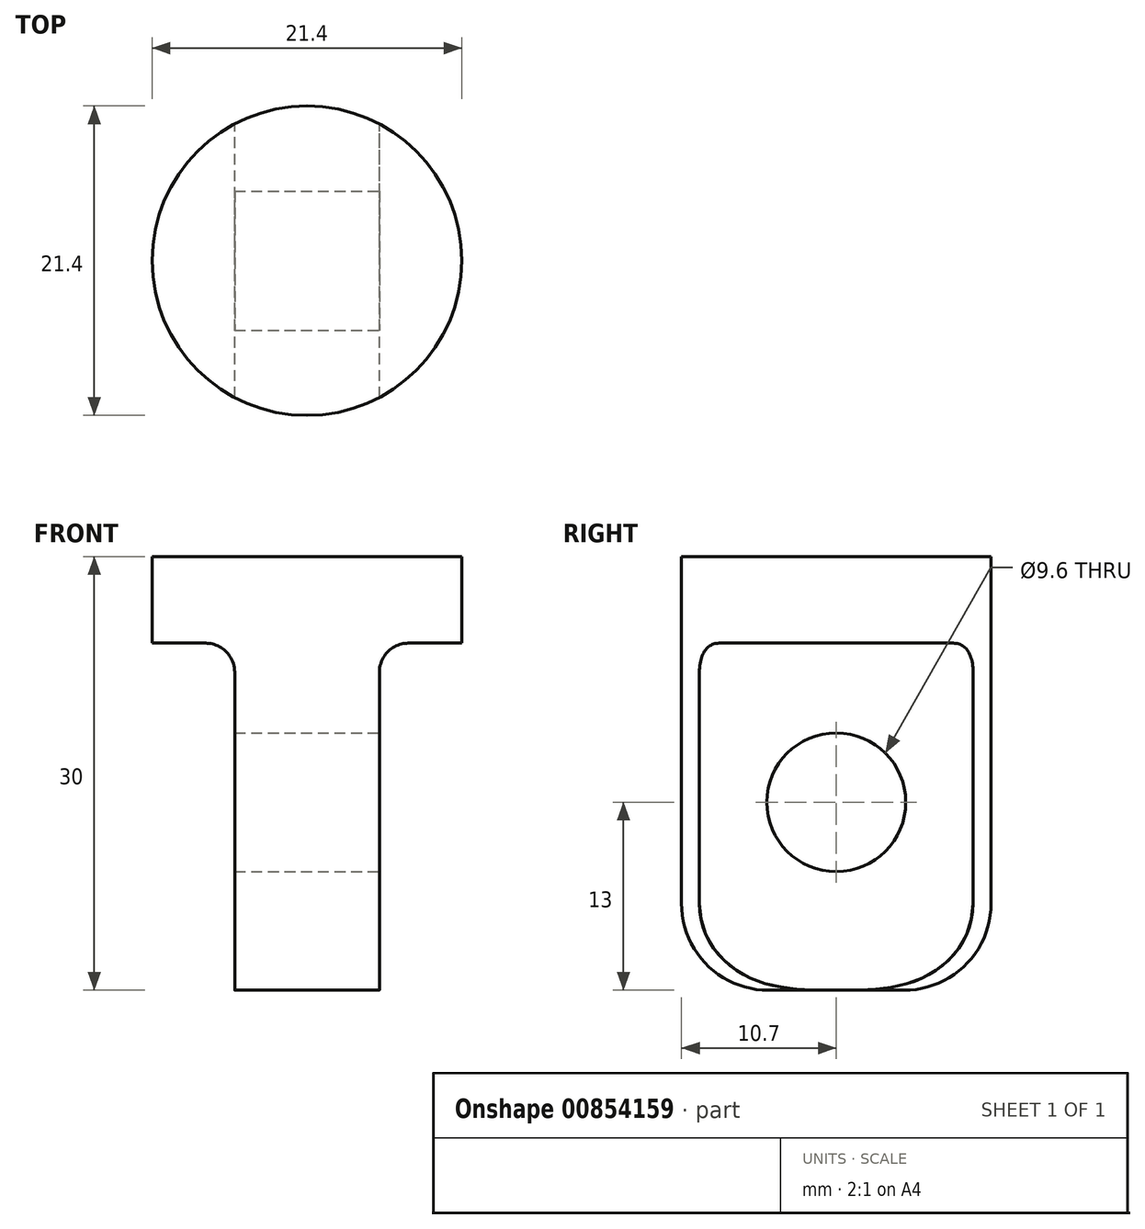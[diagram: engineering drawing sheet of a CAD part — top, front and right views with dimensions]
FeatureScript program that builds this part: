
annotation { "Feature Type Name" : "Feature", "Feature Type Description" : "" }
export const myFeature = defineFeature(function(context is Context, id is Id, definition is map)
    precondition{}
    {
        {
            var Q0;
            Q0=qCreatedBy(makeId("Top.planeOp"),FACE);
            var sketch = newSketch(context, id + "F0", { "sketchPlane" : qUnion([Q0])});
            skCircle(sketch, "E0", {"center": v(0, 0) * mm, "radius": 10.7 * mm});
            skSolve(sketch);
        }
        {
            var Q0;
            Q0=makeQuery(id+"F0.imprint","IMPRINT",FACE,{"disambiguationData":[TD([[makeQuery(id+"F0.imprint","IMPRINT",EDGE,{"derivedFrom":sQuery(id+"F0.wireOp",EDGE,"E0")}),1.0]])]});
            extrude(context, id + "F1", {"entities" : qUnion([Q0]), "oppositeDirection" : true, "depth" : 30 * mm, "offsetDistance" : 25 * mm});
        }
        {
            var Q0;
            Q0=makeQuery(id+"F1.opExtrude","CAP_EDGE",EDGE,{"disambiguationData":[OSD([sQuery(id+"F0.wireOp",EDGE,"E0")])],"isStart":false});
            fillet(context, id + "F2", {"entities" : qUnion([Q0]), "radius" : 6 * mm, "tangentPropagation" : true, "allowEdgeOverflow" : false});
        }
        {
            var Q0;
            Q0=qCreatedBy(makeId("Right.planeOp"),FACE);
            var sketch = newSketch(context, id + "F3", { "sketchPlane" : qUnion([Q0])});
            skLineSegment(sketch, "E1", {"start": v(0, -17) * mm, "end": v(0, 0) * mm});
            skCircle(sketch, "E2", {"center": v(0, -17) * mm, "radius": 4.8 * mm});
            skSolve(sketch);
        }
        {
            var Q0;
            Q0=qSketchRegion(id+"F3",true);
            extrude(context, id + "F4", {"entities" : qUnion([Q0]), "operationType" : NewBodyOperationType.REMOVE, "endBound" : BoundingType.THROUGH_ALL, "oppositeDirection" : true, "depth" : 25 * mm, "offsetDistance" : 25 * mm});
        }
        {
            var Q0;
            Q0=makeQuery(id+"F4.boolean.opBoolean","COPY",FACE,{"derivedFrom":makeQuery(id+"F4.opExtrude","CAP_FACE",FACE,{"disambiguationData":[OSD([sQuery(id+"F3.wireOp",EDGE,"E2")])],"isStart":true})});
            extrude(context, id + "F5", {"entities" : qUnion([Q0]), "operationType" : NewBodyOperationType.REMOVE, "endBound" : BoundingType.THROUGH_ALL, "oppositeDirection" : true, "depth" : 25 * mm, "offsetDistance" : 25 * mm});
        }
        {
            var Q0;
            Q0=makeQuery(id+"F1.opExtrude","CAP_FACE",FACE,{"disambiguationData":[OSD([sQuery(id+"F0.wireOp",EDGE,"E0")])],"isStart":false});
            var sketch = newSketch(context, id + "F6", { "sketchPlane" : qUnion([Q0])});
            skLineSegment(sketch, "E3.bottom", {"start": v(5, 20) * mm, "end": v(-5, 20) * mm});
            skLineSegment(sketch, "E3.top", {"start": v(5, -20) * mm, "end": v(-5, -20) * mm});
            skLineSegment(sketch, "E3.left", {"start": v(5, 20) * mm, "end": v(5, -20) * mm});
            skLineSegment(sketch, "E3.right", {"start": v(-5, 20) * mm, "end": v(-5, -20) * mm});
            skPoint(sketch, "E3.middle", {"position": v(0, 0) * mm});
            skLineSegment(sketch, "E4.bottom", {"start": v(5, 20) * mm, "end": v(11.8, 20) * mm});
            skLineSegment(sketch, "E4.top", {"start": v(5, -20) * mm, "end": v(11.8, -20) * mm});
            skLineSegment(sketch, "E4.right", {"start": v(11.8, 20) * mm, "end": v(11.8, -20) * mm});
            skLineSegment(sketch, "E5.bottom", {"start": v(-5, 20) * mm, "end": v(-11.25, 20) * mm});
            skLineSegment(sketch, "E5.top", {"start": v(-5, -16.95) * mm, "end": v(-11.25, -16.95) * mm});
            skLineSegment(sketch, "E5.left", {"start": v(-5, 20) * mm, "end": v(-5, -16.95) * mm});
            skLineSegment(sketch, "E5.right", {"start": v(-11.25, 20) * mm, "end": v(-11.25, -16.95) * mm});
            skSolve(sketch);
        }
        {
            var Q0;
            {var subQ0=sQuery(id+"F6.wireOp",EDGE,"E5.bottom");Q0=makeQuery(id+"F6.imprint","IMPRINT",FACE,{"disambiguationData":[TD([[makeQuery(id+"F6.imprint","IMPRINT",EDGE,{"derivedFrom":subQ0}),1.0]])]});}
            var Q1;
            Q1=makeQuery(id+"F6.imprint","IMPRINT",FACE,{"disambiguationData":[TD([[makeQuery(id+"F6.imprint","IMPRINT",EDGE,{"derivedFrom":sQuery(id+"F6.wireOp",EDGE,"E3.left")}),1.0]])]});
            extrude(context, id + "F7", {"entities" : qUnion([Q0, Q1]), "operationType" : NewBodyOperationType.REMOVE, "oppositeDirection" : true, "depth" : 24 * mm, "offsetDistance" : 25 * mm});
        }
        {
            var Q0;
            Q0=makeQuery(id+"F7.boolean.opBoolean","COPY",EDGE,{"derivedFrom":makeQuery(id+"F7.opExtrude","CAP_EDGE",EDGE,{"disambiguationData":[OSD([sQuery(id+"F6.wireOp",EDGE,"E3.right")])],"isStart":false})});
            var Q1;
            Q1=makeQuery(id+"F7.boolean.opBoolean","COPY",EDGE,{"derivedFrom":makeQuery(id+"F7.opExtrude","CAP_EDGE",EDGE,{"disambiguationData":[OSD([sQuery(id+"F6.wireOp",EDGE,"E3.left")])],"isStart":false})});
            fillet(context, id + "F8", {"entities" : qUnion([Q0, Q1]), "radius" : 2 * mm, "tangentPropagation" : true, "allowEdgeOverflow" : false});
        }
    });
